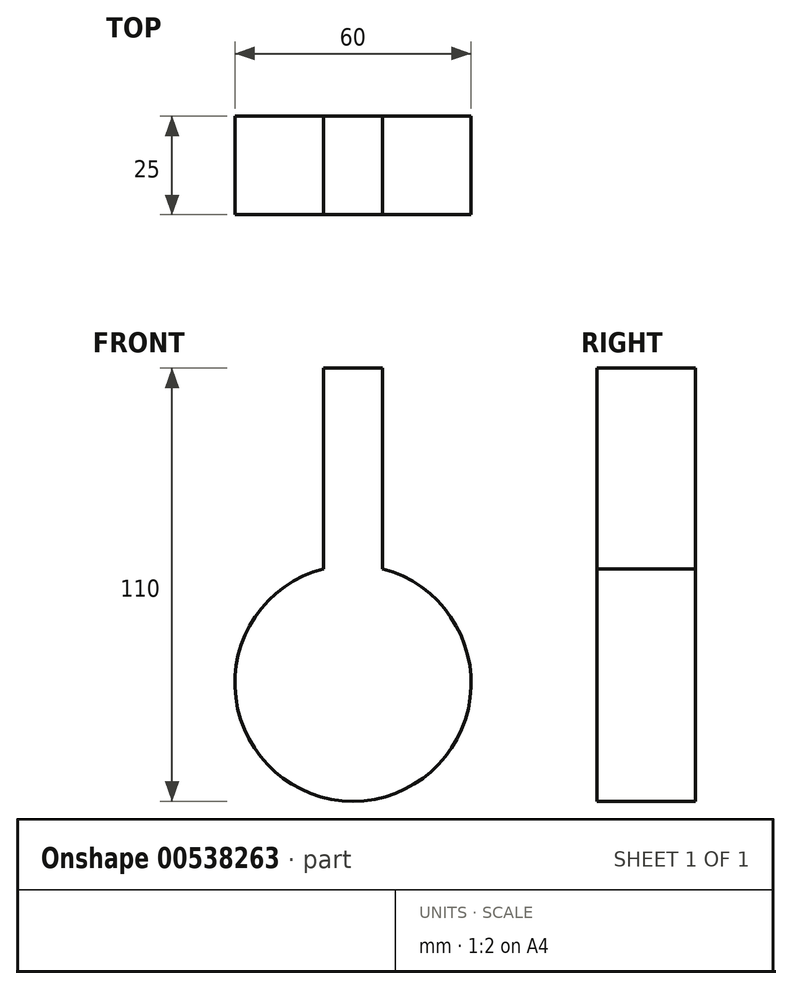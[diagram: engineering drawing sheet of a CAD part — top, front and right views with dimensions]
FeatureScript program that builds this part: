
annotation { "Feature Type Name" : "Feature", "Feature Type Description" : "" }
export const myFeature = defineFeature(function(context is Context, id is Id, definition is map)
    precondition{}
    {
        {
            var Q0;
            Q0=qCreatedBy(makeId("Front.planeOp"),FACE);
            var sketch = newSketch(context, id + "F0", { "sketchPlane" : qUnion([Q0])});
            skArc(sketch, "E0", {"start": v(-7.5, 29.05) * mm, "mid": v(0, -30) * mm, "end": v(7.5, 29.05) * mm});
            skLineSegment(sketch, "E1.bottom", {"start": v(-7.5, 80) * mm, "end": v(7.5, 80) * mm});
            skLineSegment(sketch, "E1.left", {"start": v(-7.5, 80) * mm, "end": v(-7.5, 29.05) * mm});
            skLineSegment(sketch, "E1.right", {"start": v(7.5, 80) * mm, "end": v(7.5, 29.05) * mm});
            skSolve(sketch);
        }
        {
            var Q0;
            Q0=makeQuery(id+"F0.imprint","IMPRINT",FACE,{"disambiguationData":[TD([[makeQuery(id+"F0.imprint","IMPRINT",EDGE,{"derivedFrom":sQuery(id+"F0.wireOp",EDGE,"E0")}),1.0]])]});
            extrude(context, id + "F1", {"entities" : qUnion([Q0]), "depth" : 25 * mm, "offsetDistance" : 25 * mm});
        }
    });
